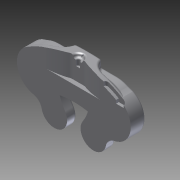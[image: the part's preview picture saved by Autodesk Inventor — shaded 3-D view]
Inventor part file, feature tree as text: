
AUTODESK INVENTOR PART (.ipt)
format: ipt  version: 2012 SP1 (Build 160190100, 190)  size: 1,366,528 bytes
history: native  units: in
note: dims shown in document units (in); Inventor stores cm internally (conversion verified against a paired STEP export)
features: sketch x46, extrude x45, fillet x12
ambient origin geometry x8: Origin, YZ Plane, XZ Plane, XY Plane, X Axis, Y Axis, Z Axis, Center Point
bodies: Solid1 (feature_tree)
feature tree (103):
  extrude  "Extrusion1"  Depth=0.44in TaperAngle=0.0deg
  extrude  "Extrusion2"  Depth=0.44in
  extrude  "Extrusion3"  Depth=0.075in
  sketch  "Sketch4"  dims[d12=0.11in d13=0.19in]
  extrude  "Extrusion4"  Depth=0.19in
  extrude  "Extrusion5"  Depth=1.44in TaperAngle=0.0deg
  fillet  "Fillet1"  Radius=0.1in
  extrude  "Extrusion6"  Depth=2.3in
  extrude  "Extrusion7"  Depth=1.09in
  extrude  "Extrusion8"  Depth=0.34in TaperAngle=0.0deg
  extrude  "Extrusion9"  Depth=0.34in TaperAngle=0.0deg
  extrude  "Extrusion10"  Depth=0.34in TaperAngle=0.0deg
  extrude  "Extrusion11"  Depth=0.5in
  sketch  "Sketch14"  dims[d52=0.6in d53=0.042in]
  fillet  "Fillet2"  Radius=1.0in
  fillet  "Fillet3"  Radius=0.75in
  fillet  "Fillet4"  Radius=1.0in
  fillet  "Fillet5"  Radius=0.075in
  extrude  "Extrusion12"  TaperAngle=0.0deg  [1 undecoded]
  extrude  "Extrusion13"  Depth=0.042in
  extrude  "Extrusion14"  Depth=0.125in TaperAngle=0.0deg
  extrude  "Extrusion15"  Depth=0.75in TaperAngle=0.0deg
  fillet  "Fillet6"  Radius=0.1in
  fillet  "Fillet7"  Radius=0.75in
  extrude  "Extrusion16"  Depth=0.75in TaperAngle=0.0deg
  extrude  "Extrusion17"  Depth=1.0in TaperAngle=0.0deg
  extrude  "Extrusion18"  Depth=0.125in
  extrude  "Extrusion19"  Depth=0.25in TaperAngle=0.0deg
  extrude  "Extrusion20"  Depth=1.25in TaperAngle=0.0deg
  extrude  "Extrusion21"  Depth=1.0in
  extrude  "Extrusion22"  Depth=0.25in TaperAngle=0.0deg
  extrude  "Extrusion23"  Depth=0.25in TaperAngle=0.0deg
  extrude  "Extrusion24"  Depth=2.0in TaperAngle=0.0deg
  extrude  "Extrusion25"  Depth=1.215in TaperAngle=0.0deg
  extrude  "Extrusion26"  Depth=1.215in TaperAngle=0.0deg
  extrude  "Extrusion27"  Depth=1.215in TaperAngle=0.0deg
  extrude  "Extrusion28"  Depth=1.215in TaperAngle=0.0deg
  extrude  "Extrusion29"  Depth=0.1in
  extrude  "Extrusion30"  Depth=0.1in
  extrude  "Extrusion31"  Depth=0.1in
  extrude  "Extrusion32"  [1 undecoded]
  extrude  "Extrusion33"  [1 undecoded]
  extrude  "Extrusion34"  [1 undecoded]
  extrude  "Extrusion35"  [1 undecoded]
  extrude  "Extrusion37"  [1 undecoded]
  extrude  "Extrusion38"  [1 undecoded]
  extrude  "Extrusion39"  [1 undecoded]
  extrude  "Extrusion40"  [1 undecoded]
  extrude  "Extrusion41"  [1 undecoded]
  extrude  "Extrusion42"  [1 undecoded]
  extrude  "Extrusion43"  [1 undecoded]
  extrude  "Extrusion44"  [1 undecoded]
  extrude  "Extrusion45"  [1 undecoded]
  extrude  "Extrusion46"  [1 undecoded]
  fillet  "Fillet8"  [1 undecoded]
  fillet  "Fillet9"  [1 undecoded]
  fillet  "Fillet10"  [1 undecoded]
  fillet  "Fillet11"  [1 undecoded]
  fillet  "Fillet12"  [1 undecoded]
  sketch  "Sketch1"  dims[d0=1.9in d1=1.18in d2=0.44in d3=0.0in]
  sketch  "Sketch2"  dims[d6=1.0in d7=0.0in d8=0.44in]
  sketch  "Sketch3"  dims[d9=0.15in d10=0.0in d11=0.075in]
  sketch  "Sketch5"  dims[d14=0.25in d15=0.0in d17=1.44in d18=0.0in d19=0.1in]
  sketch  "Sketch7"  dims[d20=0.238in d21=2.3in]
  sketch  "Sketch8"  dims[d24=0.6in d25=1.09in]
  sketch  "Sketch9"  dims[d26=0.34in d27=0.0in d28=0.34in d29=0.0in]
  sketch  "Sketch10"  dims[d30=0.34in d31=0.0in d33=0.34in d34=0.0in]
  sketch  "Sketch11"  dims[d35=0.34in d36=0.0in d37=0.34in d38=0.0in]
  sketch  "Sketch12"  dims[d40=1.0in d41=0.5in d42=1.0in d43=0.75in d44=1.0in d45=0.0in d46=0.075in d47=0.0in]
  sketch  "Sketch13"  dims[d48=1.0in d49=0.0in d50=0.0in d51=0.0in]
  sketch  "Sketch15"  dims[d55=0.125in d56=0.0in d57=0.125in d58=0.0in]
  sketch  "Sketch16"  dims[d59=0.2in d60=0.0in d61=0.75in d62=0.0in d63=0.1in d64=0.0in d65=0.75in d66=0.0in]
  sketch  "Sketch17"  dims[d67=0.75in d68=0.0in d69=0.75in d70=0.0in]
  sketch  "Sketch19"  dims[d71=0.75in d72=0.0in d73=1.0in d74=0.0in]
  sketch  "Sketch20"  dims[d75=0.93in d76=0.125in]
  sketch  "Sketch21"  dims[d77=1.0in d78=0.0in d79=0.25in d80=0.0in]
  sketch  "Sketch22"  dims[d81=0.25in d82=0.0in d83=1.25in d84=0.0in]
  sketch  "Sketch23"  dims[d85=0.25in d86=0.0in d92=1.0in]
  sketch  "Sketch24"  dims[d93=0.25in d94=0.0in d95=0.25in d96=0.0in]
  sketch  "Sketch25"  dims[d97=0.25in d98=0.0in d99=0.25in d100=0.0in]
  sketch  "Sketch26"  dims[d101=0.25in d102=0.0in d105=2.0in d106=0.0in]
  sketch  "Sketch27"  dims[d108=1.215in d109=0.0in d110=1.215in d111=0.0in]
  sketch  "Sketch28"  dims[d112=1.215in d113=0.0in d114=1.215in d115=0.0in]
  sketch  "Sketch29"  dims[d116=1.215in d117=0.0in d118=1.215in d119=0.0in]
  sketch  "Sketch30"  dims[d120=1.215in d121=0.0in d122=1.215in d123=0.0in]
  sketch  "Sketch32"  dims[d124=5.0in d125=0.0in d126=0.1in]
  sketch  "Sketch33"  dims[d127=0.1in d128=0.1in]
  sketch  "Sketch34"  dims[d129=0.1in d130=0.1in]
  sketch  "Sketch35"
  sketch  "Sketch36"
  sketch  "Sketch37"
  sketch  "Sketch38"
  sketch  "Sketch39"
  sketch  "Sketch41"
  sketch  "Sketch42"
  sketch  "Sketch43"
  sketch  "Sketch44"
  sketch  "Sketch45"
  sketch  "Sketch46"
  sketch  "Sketch47"
  sketch  "Sketch48"
  sketch  "Sketch49"
  sketch  "Sketch51"
note: 20 required parameter values undecoded (feature->parameter linkage not recoverable at this tier; creation-order binding heuristic only, values carry confidence <= 0.55)
